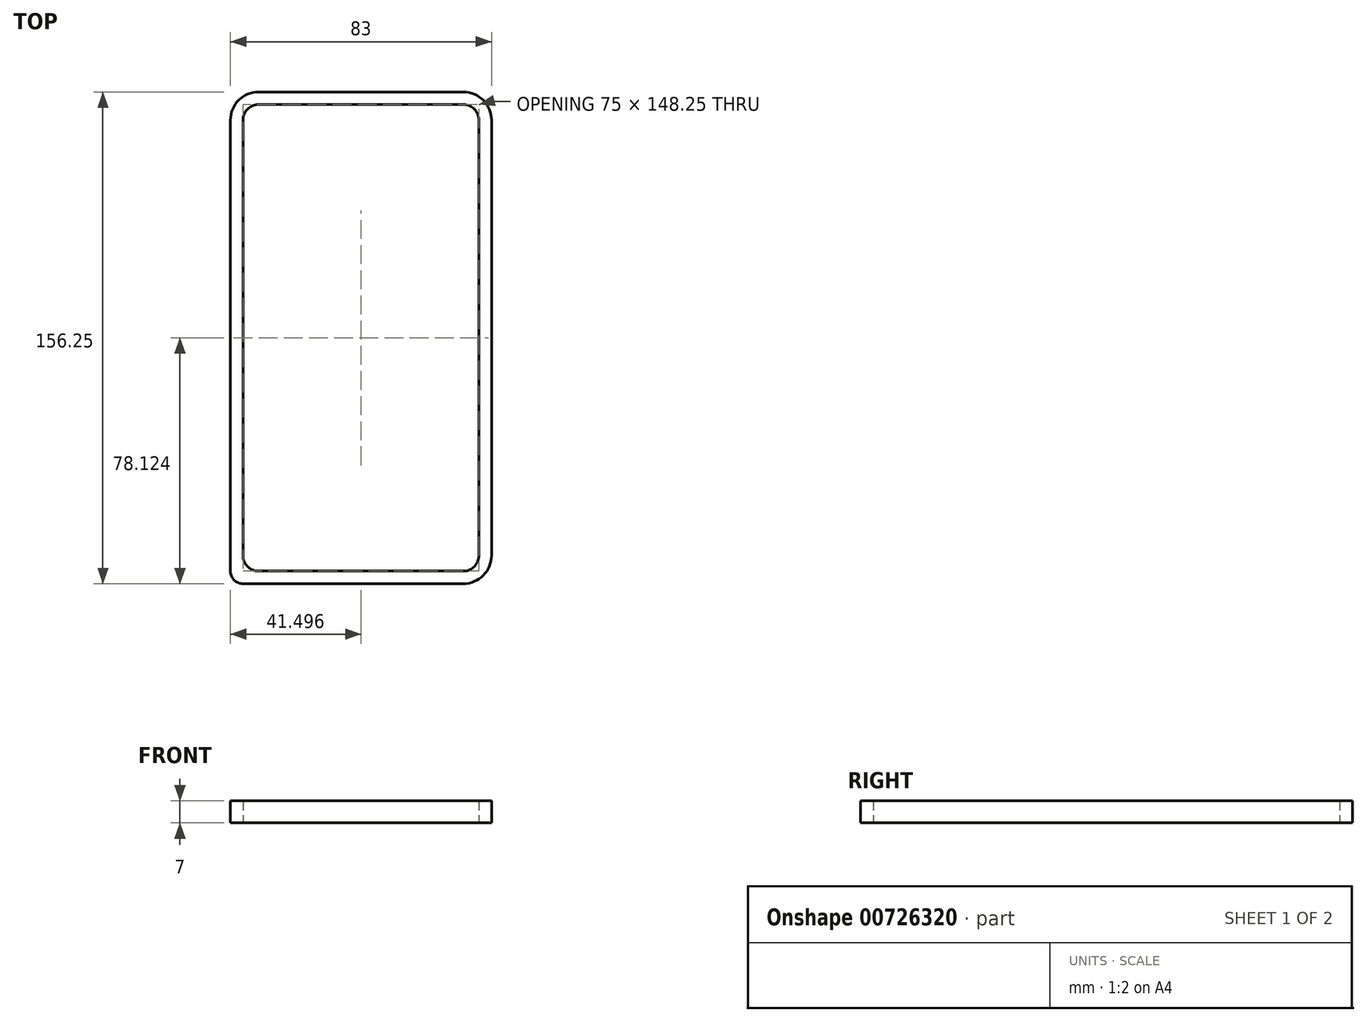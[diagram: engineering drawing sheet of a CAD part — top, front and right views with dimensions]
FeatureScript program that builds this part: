
annotation { "Feature Type Name" : "Feature", "Feature Type Description" : "" }
export const myFeature = defineFeature(function(context is Context, id is Id, definition is map)
    precondition{}
    {
        {
            var Q0;
            Q0=qCreatedBy(makeId("Top.planeOp"),FACE);
            var sketch = newSketch(context, id + "F0", { "sketchPlane" : qUnion([Q0])});
            skLineSegment(sketch, "E0.bottom", {"start": v(-33.31, 64.96) * mm, "end": v(31.69, 64.96) * mm});
            skLineSegment(sketch, "E0.top", {"start": v(-33.31, -83.3) * mm, "end": v(31.69, -83.3) * mm});
            skLineSegment(sketch, "E0.left", {"start": v(-38.31, 59.96) * mm, "end": v(-38.31, -78.3) * mm});
            skLineSegment(sketch, "E0.right", {"start": v(36.69, 59.96) * mm, "end": v(36.69, -78.3) * mm});
            skPoint(sketch, "E1.visualSharp", {"position": v(-38.31, 64.96) * mm});
            skArc(sketch, "E1.filletArc", {"start": v(-33.31, 64.96) * mm, "mid": v(-36.85, 63.5) * mm, "end": v(-38.31, 59.96) * mm});
            skPoint(sketch, "E2.visualSharp", {"position": v(36.69, 64.96) * mm});
            skArc(sketch, "E2.filletArc", {"start": v(36.69, 59.96) * mm, "mid": v(35.22, 63.5) * mm, "end": v(31.69, 64.96) * mm});
            skPoint(sketch, "E3.visualSharp", {"position": v(36.69, -83.3) * mm});
            skArc(sketch, "E3.filletArc", {"start": v(31.69, -83.3) * mm, "mid": v(35.22, -81.83) * mm, "end": v(36.69, -78.3) * mm});
            skPoint(sketch, "E4.visualSharp", {"position": v(-38.31, -83.3) * mm});
            skArc(sketch, "E4.filletArc", {"start": v(-38.31, -78.3) * mm, "mid": v(-36.85, -81.83) * mm, "end": v(-33.31, -83.3) * mm});
            skLineSegment(sketch, "E5.0", {"start": v(-42.31, 59.96) * mm, "end": v(-42.31, -83.3) * mm});
            skArc(sketch, "E5.1", {"start": v(-33.31, 68.96) * mm, "mid": v(-39.68, 66.33) * mm, "end": v(-42.31, 59.96) * mm});
            skLineSegment(sketch, "E5.2", {"start": v(-33.31, 68.96) * mm, "end": v(31.69, 68.96) * mm});
            skLineSegment(sketch, "E5.3", {"start": v(-38.31, -87.3) * mm, "end": v(31.69, -87.3) * mm});
            skArc(sketch, "E5.4", {"start": v(31.69, -87.3) * mm, "mid": v(38.05, -84.66) * mm, "end": v(40.69, -78.3) * mm});
            skLineSegment(sketch, "E5.5", {"start": v(40.69, 59.96) * mm, "end": v(40.69, -78.3) * mm});
            skArc(sketch, "E5.6", {"start": v(40.69, 59.96) * mm, "mid": v(38.05, 66.33) * mm, "end": v(31.69, 68.96) * mm});
            skArc(sketch, "E6", {"start": v(-42.31, -83.3) * mm, "mid": v(-41.14, -86.12) * mm, "end": v(-38.31, -87.3) * mm});
            skSolve(sketch);
        }
        {
            var Q0;
            Q0=makeQuery(id+"F0.imprint","IMPRINT",FACE,{"disambiguationData":[TD([[makeQuery(id+"F0.imprint","IMPRINT",EDGE,{"derivedFrom":sQuery(id+"F0.wireOp",EDGE,"E0.bottom")}),1.0]])]});
            extrude(context, id + "F1", {"entities" : qUnion([Q0]), "depth" : 7 * mm, "offsetDistance" : 25 * mm});
        }
    });
